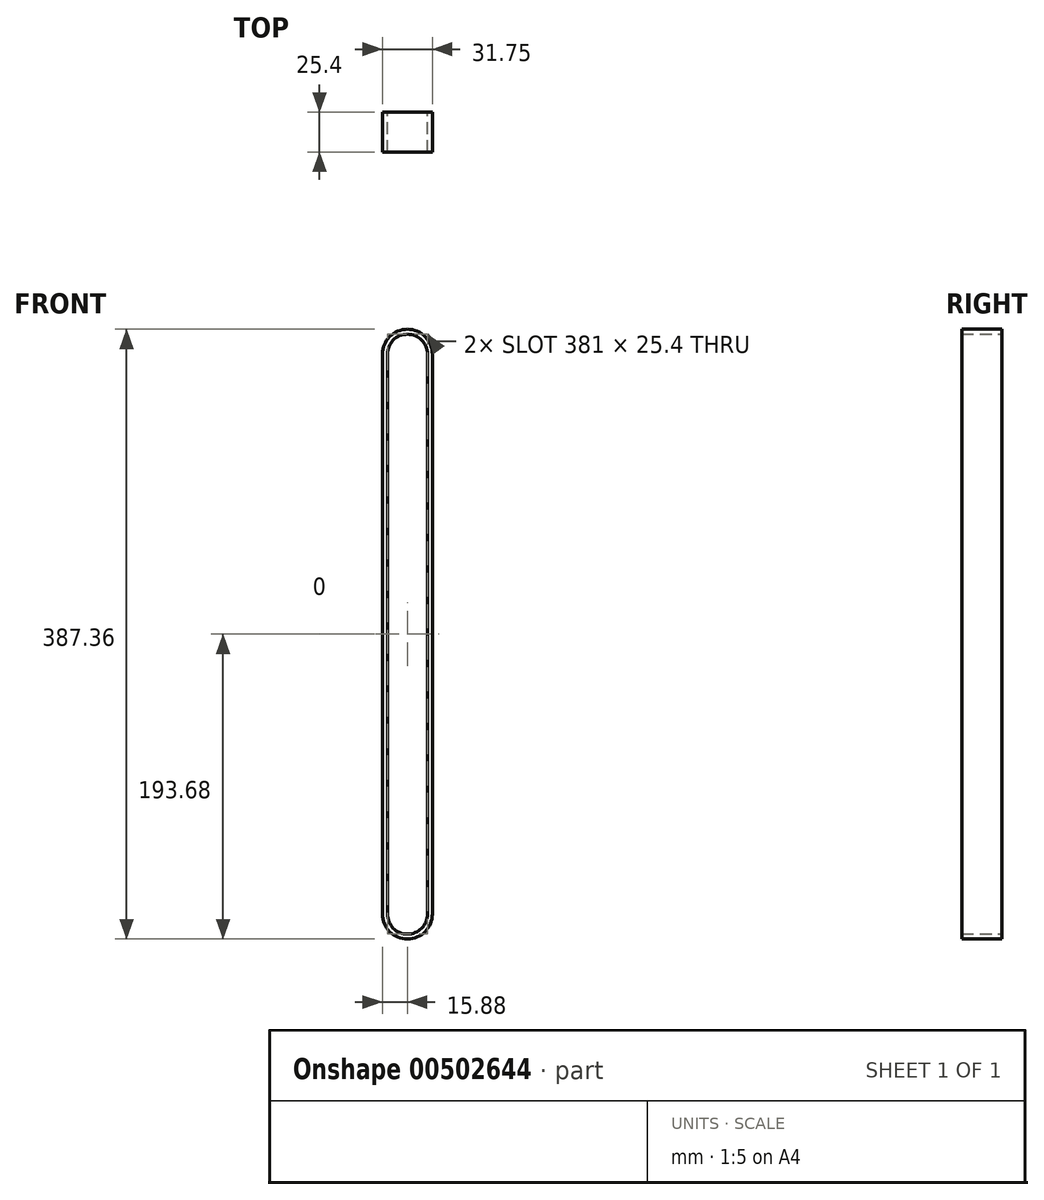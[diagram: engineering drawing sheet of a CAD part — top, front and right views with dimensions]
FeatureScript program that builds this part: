
annotation { "Feature Type Name" : "Feature", "Feature Type Description" : "" }
export const myFeature = defineFeature(function(context is Context, id is Id, definition is map)
    precondition{}
    {
        {
            var Q0;
            Q0=qCreatedBy(makeId("Front.planeOp"),FACE);
            var sketch = newSketch(context, id + "F0", { "sketchPlane" : qUnion([Q0])});
            skLineSegment(sketch, "E0", {"start": v(0, 0) * mm, "end": v(0, -355.6) * mm});
            skLineSegment(sketch, "E1", {"start": v(25.4, 0) * mm, "end": v(25.4, -355.6) * mm});
            skArc(sketch, "E2", {"start": v(25.4, 0) * mm, "mid": v(12.7, 12.7) * mm, "end": v(0, 0) * mm});
            skArc(sketch, "E3", {"start": v(0, -355.6) * mm, "mid": v(12.7, -368.3) * mm, "end": v(25.4, -355.6) * mm});
            skArc(sketch, "E4.0", {"start": v(28.58, 0) * mm, "mid": v(12.7, 15.87) * mm, "end": v(-3.17, 0) * mm});
            skLineSegment(sketch, "E4.1", {"start": v(28.57, 0) * mm, "end": v(28.58, -355.6) * mm});
            skArc(sketch, "E4.2", {"start": v(-3.17, -355.6) * mm, "mid": v(12.7, -371.48) * mm, "end": v(28.58, -355.6) * mm});
            skLineSegment(sketch, "E4.3", {"start": v(-3.18, 0) * mm, "end": v(-3.17, -355.6) * mm});
            skSolve(sketch);
        }
        {
            var Q0;
            Q0=makeQuery(id+"F0.imprint","IMPRINT",FACE,{"disambiguationData":[TD([[makeQuery(id+"F0.imprint","IMPRINT",EDGE,{"derivedFrom":sQuery(id+"F0.wireOp",EDGE,"E0")}),-1.0]])]});
            extrude(context, id + "F1", {"entities" : qUnion([Q0]), "depth" : 25.4 * mm});
        }
    });
